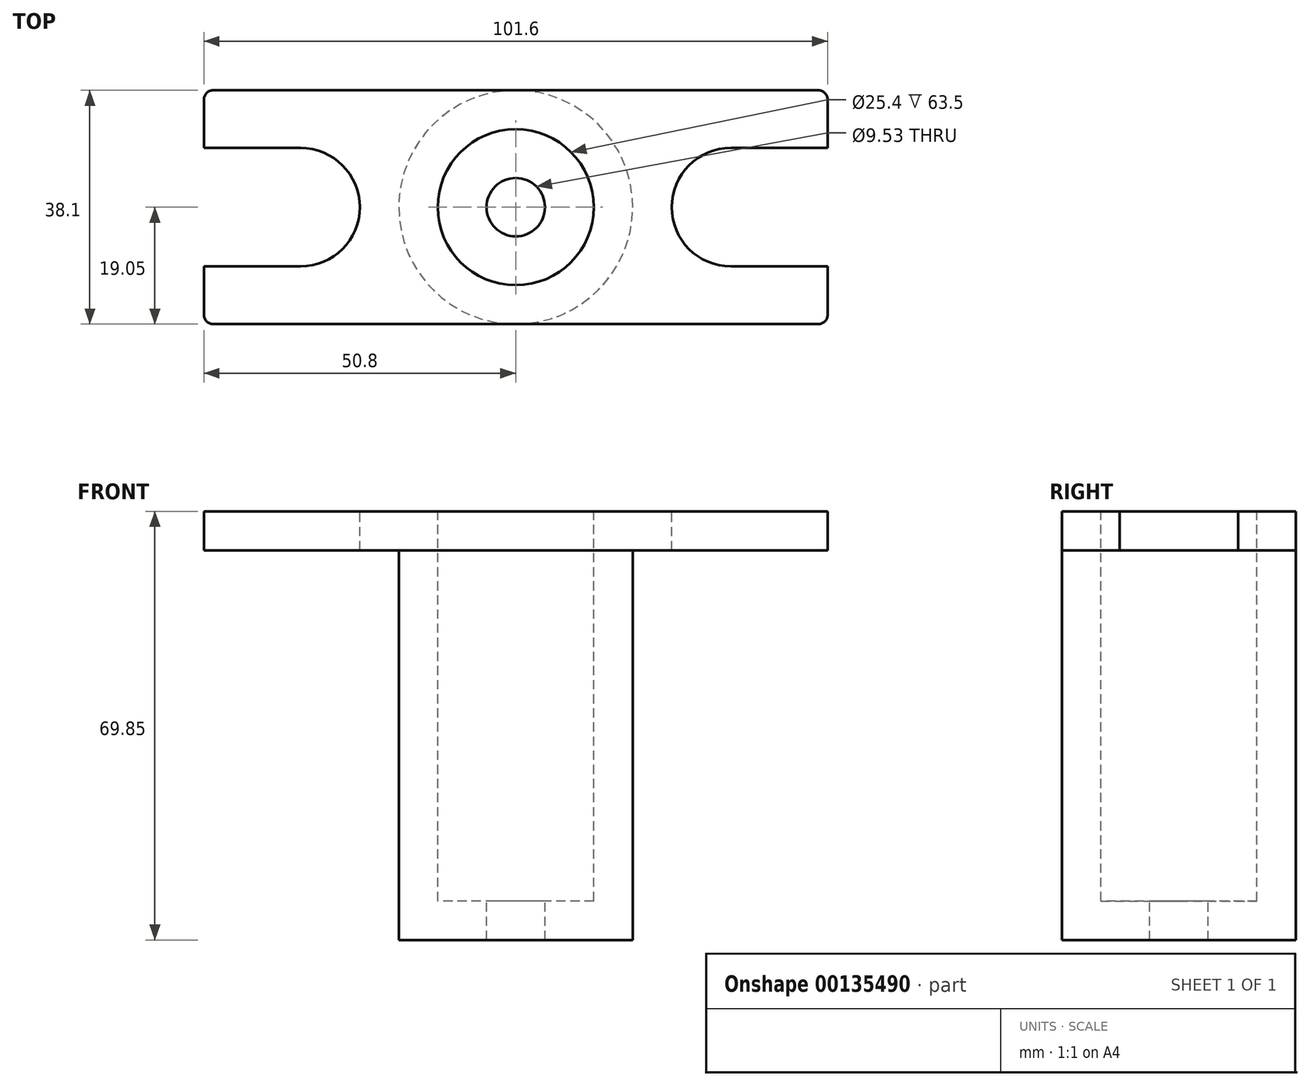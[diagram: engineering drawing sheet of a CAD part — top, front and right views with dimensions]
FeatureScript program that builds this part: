
annotation { "Feature Type Name" : "Feature", "Feature Type Description" : "" }
export const myFeature = defineFeature(function(context is Context, id is Id, definition is map)
    precondition{}
    {
        {
            var Q0;
            Q0=qCreatedBy(makeId("Front.planeOp"),FACE);
            var sketch = newSketch(context, id + "F0", { "sketchPlane" : qUnion([Q0])});
            skLineSegment(sketch, "E0.bottom", {"start": v(0, 0) * mm, "end": v(-19.05, 0) * mm});
            skLineSegment(sketch, "E0.top", {"start": v(0, -69.85) * mm, "end": v(-19.05, -69.85) * mm});
            skLineSegment(sketch, "E0.left", {"start": v(0, 0) * mm, "end": v(0, -69.85) * mm});
            skLineSegment(sketch, "E0.right", {"start": v(-19.05, 0) * mm, "end": v(-19.05, -69.85) * mm});
            skLineSegment(sketch, "E1.bottom", {"start": v(-50.8, 0) * mm, "end": v(50.8, 0) * mm});
            skLineSegment(sketch, "E1.top", {"start": v(-50.8, -6.35) * mm, "end": v(50.8, -6.35) * mm});
            skLineSegment(sketch, "E1.left", {"start": v(-50.8, 0) * mm, "end": v(-50.8, -6.35) * mm});
            skLineSegment(sketch, "E1.right", {"start": v(50.8, 0) * mm, "end": v(50.8, -6.35) * mm});
            skSolve(sketch);
        }
        {
            var Q0;
            {var subQ0=sQuery(id+"F0.wireOp",EDGE,"E0.top");Q0=makeQuery(id+"F0.imprint","IMPRINT",FACE,{"disambiguationData":[TD([[makeQuery(id+"F0.imprint","IMPRINT",EDGE,{"derivedFrom":subQ0}),-1.0]])]});}
            var Q1;
            {var subQ5=sQuery(id+"F0.wireOp",EDGE,"07zzq5kQ-JGfE-IKA0-QN8K-cusD11BXSfr4.left");Q1=makeQuery(id+"F0.imprint","IMPRINT",FACE,{"disambiguationData":[TD([[makeQuery(id+"F0.imprint","IMPRINT",EDGE,{"derivedFrom":subQ5}),-1.0]])]});}
            var Q2;
            Q2=sQuery(id+"F0.wireOp",EDGE,"E0.left");
            revolve(context, id + "F1", {"entities" : qUnion([Q0, Q1]), "axis" : qUnion([Q2]), "revolveType" : RevolveType.FULL});
        }
        {
            var Q0;
            {var subQ5=sQuery(id+"F0.wireOp",EDGE,"E1.left");Q0=makeQuery(id+"F0.imprint","IMPRINT",FACE,{"disambiguationData":[TD([[makeQuery(id+"F0.imprint","IMPRINT",EDGE,{"derivedFrom":subQ5}),1.0]])]});}
            var Q1;
            {var subQ0=sQuery(id+"F0.wireOp",EDGE,"E1.bottom");var subQ1=sQuery(id+"F0.wireOp",EDGE,"E0.left");var subQ2=makeQuery(id+"F0.imprint","INTERSECT",VERTEX,{"derivedFrom":[subQ1,subQ0]});Q1=makeQuery(id+"F0.imprint","IMPRINT",FACE,{"disambiguationData":[TD([[makeQuery(id+"F0.imprint","IMPRINT",EDGE,{"disambiguationData":[TD([[subQ2,-1.0]])],"derivedFrom":subQ1}),-1.0]])]});}
            var Q2;
            {var subQ5=sQuery(id+"F0.wireOp",EDGE,"E1.right");Q2=makeQuery(id+"F0.imprint","IMPRINT",FACE,{"disambiguationData":[TD([[makeQuery(id+"F0.imprint","IMPRINT",EDGE,{"derivedFrom":subQ5}),-1.0]])]});}
            extrude(context, id + "F2", {"entities" : qUnion([Q0, Q1, Q2]), "operationType" : NewBodyOperationType.ADD, "endBound" : BoundingType.SYMMETRIC, "depth" : 38.1 * mm});
        }
        {
            var Q0;
            Q0=qCreatedBy(makeId("Top.planeOp"),FACE);
            var sketch = newSketch(context, id + "F3", { "sketchPlane" : qUnion([Q0])});
            skCircle(sketch, "E2", {"center": v(0, 0) * mm, "radius": 12.7 * mm});
            skLineSegment(sketch, "E3", {"start": v(-50.8, 9.65) * mm, "end": v(-35.05, 9.65) * mm});
            skLineSegment(sketch, "E4", {"start": v(-50.8, -9.65) * mm, "end": v(-35.05, -9.65) * mm});
            skLineSegment(sketch, "E5", {"start": v(50.8, 9.65) * mm, "end": v(35.05, 9.65) * mm});
            skLineSegment(sketch, "E6", {"start": v(50.8, -9.65) * mm, "end": v(35.05, -9.65) * mm});
            skArc(sketch, "E7", {"start": v(-35.05, 9.65) * mm, "mid": v(-25.4, 0) * mm, "end": v(-35.05, -9.65) * mm});
            skArc(sketch, "E8", {"start": v(35.05, -9.65) * mm, "mid": v(25.4, 0) * mm, "end": v(35.05, 9.65) * mm});
            skLineSegment(sketch, "E9", {"start": v(-50.8, 9.65) * mm, "end": v(-50.8, -9.65) * mm});
            skLineSegment(sketch, "E10", {"start": v(50.8, -9.65) * mm, "end": v(50.8, 9.65) * mm});
            skCircle(sketch, "E11", {"center": v(0, 0) * mm, "radius": 4.76 * mm});
            skSolve(sketch);
        }
        {
            var Q0;
            Q0=makeQuery(id+"F3.imprint","IMPRINT",FACE,{"disambiguationData":[TD([[makeQuery(id+"F3.imprint","IMPRINT",EDGE,{"derivedFrom":sQuery(id+"F3.wireOp",EDGE,"E2")}),1.0]])]});
            extrude(context, id + "F4", {"entities" : qUnion([Q0]), "operationType" : NewBodyOperationType.REMOVE, "oppositeDirection" : true, "depth" : 63.5 * mm});
        }
        {
            var Q0;
            Q0=makeQuery(id+"F3.imprint","IMPRINT",FACE,{"disambiguationData":[TD([[makeQuery(id+"F3.imprint","IMPRINT",EDGE,{"derivedFrom":sQuery(id+"F3.wireOp",EDGE,"E3")}),-1.0]])]});
            var Q1;
            Q1=makeQuery(id+"F3.imprint","IMPRINT",FACE,{"disambiguationData":[TD([[makeQuery(id+"F3.imprint","IMPRINT",EDGE,{"derivedFrom":sQuery(id+"F3.wireOp",EDGE,"E5")}),1.0]])]});
            extrude(context, id + "F5", {"entities" : qUnion([Q0, Q1]), "operationType" : NewBodyOperationType.REMOVE, "endBound" : BoundingType.UP_TO_NEXT, "oppositeDirection" : true, "depth" : 25.4 * mm});
        }
        {
            var Q0;
            Q0=makeQuery(id+"F2.opExtrude","CAP_EDGE",EDGE,{"disambiguationData":[OSD([sQuery(id+"F0.wireOp",EDGE,"E1.right")])],"isStart":false});
            var Q1;
            Q1=makeQuery(id+"F2.opExtrude","CAP_EDGE",EDGE,{"disambiguationData":[OSD([sQuery(id+"F0.wireOp",EDGE,"E1.left")])],"isStart":false});
            var Q2;
            Q2=makeQuery(id+"F2.opExtrude","CAP_EDGE",EDGE,{"disambiguationData":[OSD([sQuery(id+"F0.wireOp",EDGE,"E1.right")])],"isStart":true});
            var Q3;
            Q3=makeQuery(id+"F2.opExtrude","CAP_EDGE",EDGE,{"disambiguationData":[OSD([sQuery(id+"F0.wireOp",EDGE,"E1.left")])],"isStart":true});
            fillet(context, id + "F6", {"entities" : qUnion([Q0, Q1, Q2, Q3]), "radius" : 1.52 * mm, "tangentPropagation" : true, "allowEdgeOverflow" : false});
        }
        {
            var Q0;
            Q0=makeQuery(id+"F3.imprint","IMPRINT",FACE,{"disambiguationData":[TD([[makeQuery(id+"F3.imprint","IMPRINT",EDGE,{"derivedFrom":sQuery(id+"F3.wireOp",EDGE,"E11")}),1.0]])]});
            extrude(context, id + "F7", {"entities" : qUnion([Q0]), "operationType" : NewBodyOperationType.REMOVE, "endBound" : BoundingType.THROUGH_ALL, "oppositeDirection" : true, "depth" : 25.4 * mm});
        }
    });
